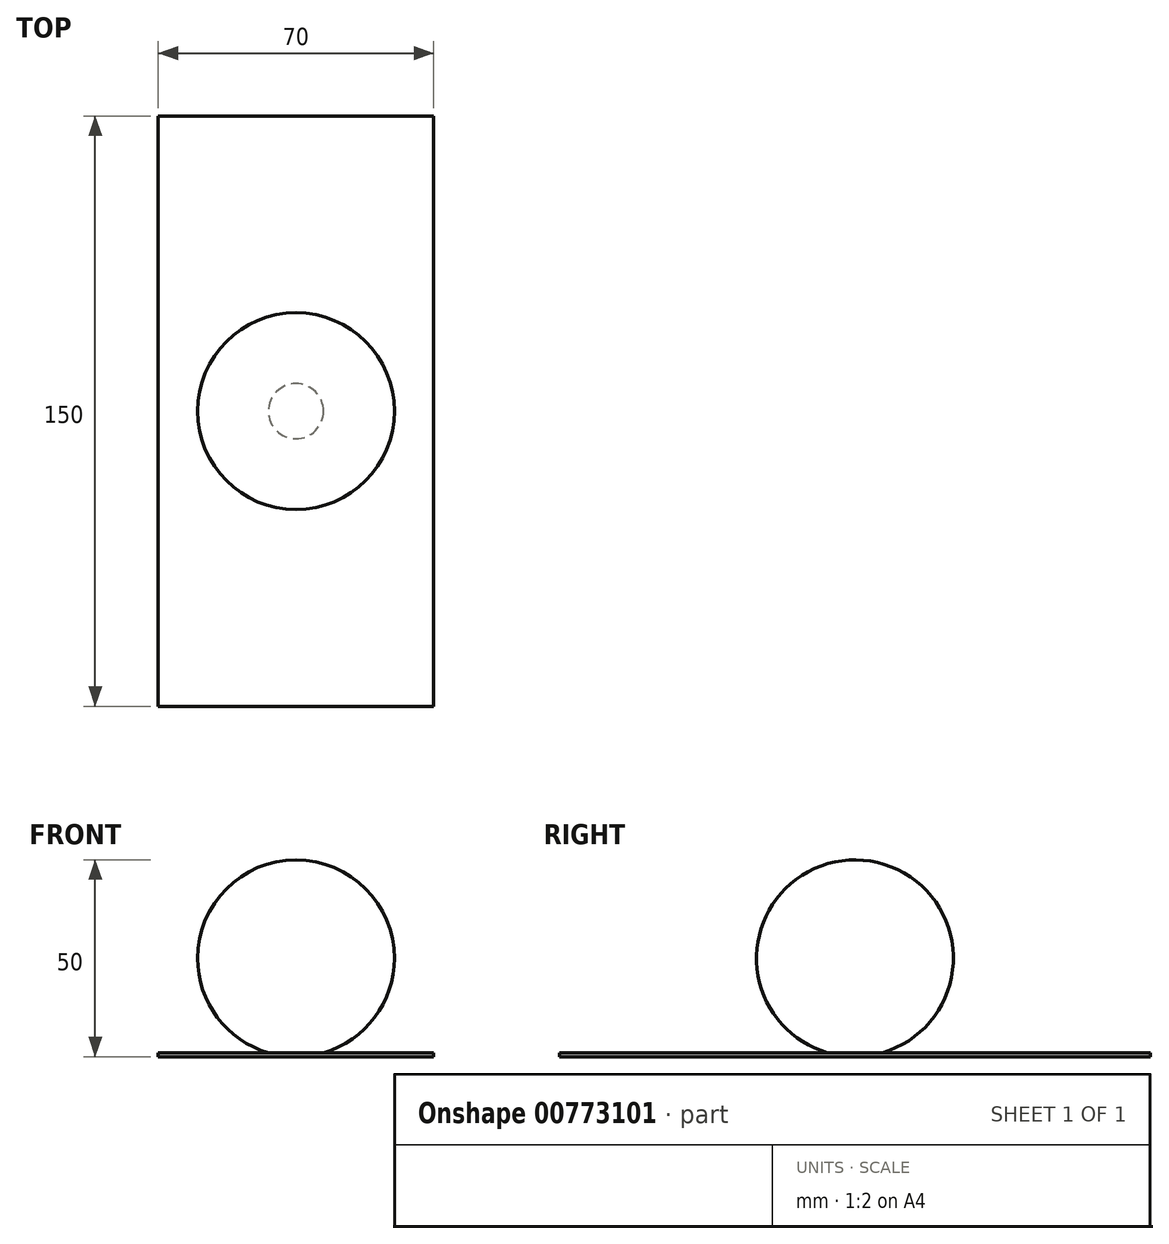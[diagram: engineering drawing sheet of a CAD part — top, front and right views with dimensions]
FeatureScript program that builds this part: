
annotation { "Feature Type Name" : "Feature", "Feature Type Description" : "" }
export const myFeature = defineFeature(function(context is Context, id is Id, definition is map)
    precondition{}
    {
        {
            var Q0;
            Q0=qCreatedBy(makeId("Top.planeOp"),FACE);
            var sketch = newSketch(context, id + "F0", { "sketchPlane" : qUnion([Q0])});
            skArc(sketch, "E0", {"start": v(-25, 0) * mm, "mid": v(0, -25) * mm, "end": v(25, 0) * mm});
            skLineSegment(sketch, "E1", {"start": v(25, 0) * mm, "end": v(-50.3, 0) * mm});
            skSolve(sketch);
        }
        {
            var Q0;
            Q0 = qSketchRegion(id + "F0", true);
            var Q1;
            Q1=sQuery(id+"F0.wireOp",EDGE,"E1");
            revolve(context, id + "F1", {"surfaceOperationType" : NewSurfaceOperationType.NEW, "entities" : qUnion([Q0]), "axis" : qUnion([Q1]), "revolveType" : RevolveType.FULL});
        }
        {
            var Q0;
            Q0=qCreatedBy(makeId("Top.planeOp"),FACE);
            cPlane(context, id + "F2", {"entities" : qUnion([Q0]), "cplaneType" : CPlaneType.OFFSET, "offset" : 25 * mm, "oppositeDirection" : true, "width" : 150 * mm, "height" : 150 * mm});
        }
        {
            var Q0;
            Q0=qCreatedBy(id+"F2.planeOp",FACE);
            var sketch = newSketch(context, id + "F3", { "sketchPlane" : qUnion([Q0])});
            skLineSegment(sketch, "E2.bottom", {"start": v(35, 75) * mm, "end": v(-35, 75) * mm});
            skLineSegment(sketch, "E2.top", {"start": v(35, -75) * mm, "end": v(-35, -75) * mm});
            skLineSegment(sketch, "E2.left", {"start": v(35, 75) * mm, "end": v(35, -75) * mm});
            skLineSegment(sketch, "E2.right", {"start": v(-35, 75) * mm, "end": v(-35, -75) * mm});
            skSolve(sketch);
        }
        {
            var Q0;
            Q0=makeQuery(id+"F3.imprint","IMPRINT",FACE,{"disambiguationData":[TD([[makeQuery(id+"F3.imprint","IMPRINT",EDGE,{"derivedFrom":sQuery(id+"F3.wireOp",EDGE,"E2.bottom")}),1.0]])]});
            extrude(context, id + "F4", {"entities" : qUnion([Q0]), "operationType" : NewBodyOperationType.ADD, "depth" : 1 * mm, "offsetDistance" : 25 * mm});
        }
        {
            var Q0;
            Q0=qCreatedBy(makeId("Top.planeOp"),FACE);
            cPlane(context, id + "F5", {"entities" : qUnion([Q0]), "cplaneType" : CPlaneType.OFFSET, "offset" : 75 * mm, "width" : 150 * mm, "height" : 150 * mm});
        }
        {
            var Q0;
            Q0=qCreatedBy(id+"F5.planeOp",FACE);
            var sketch = newSketch(context, id + "F6", { "sketchPlane" : qUnion([Q0])});
            skLineSegment(sketch, "E3.bottom", {"start": v(50, 100) * mm, "end": v(-50, 100) * mm});
            skLineSegment(sketch, "E3.top", {"start": v(50, -100) * mm, "end": v(-50, -100) * mm});
            skLineSegment(sketch, "E3.left", {"start": v(50, 100) * mm, "end": v(50, -100) * mm});
            skLineSegment(sketch, "E3.right", {"start": v(-50, 100) * mm, "end": v(-50, -100) * mm});
            skSolve(sketch);
        }
        {
            var Q0;
            Q0=sQuery(id+"F6.wireOp",VERTEX,"E3.bottom.end");
            var Q1;
            Q1=makeQuery(id+"F4.opExtrude","CAP_VERTEX",VERTEX,{"disambiguationData":[OSD([sQuery(id+"F3.wireOp",EDGE,"E2.bottom"),sQuery(id+"F3.wireOp",EDGE,"E2.right")])],"isStart":true});
            var Q2;
            Q2=makeQuery(id+"F4.opExtrude","CAP_VERTEX",VERTEX,{"disambiguationData":[OSD([sQuery(id+"F3.wireOp",EDGE,"E2.bottom"),sQuery(id+"F3.wireOp",EDGE,"E2.left")])],"isStart":true});
            cPlane(context, id + "F7", {"entities" : qUnion([Q0, Q1, Q2]), "cplaneType" : CPlaneType.THREE_POINT, "offset" : 25 * mm, "width" : 150 * mm, "height" : 150 * mm});
        }
    });
